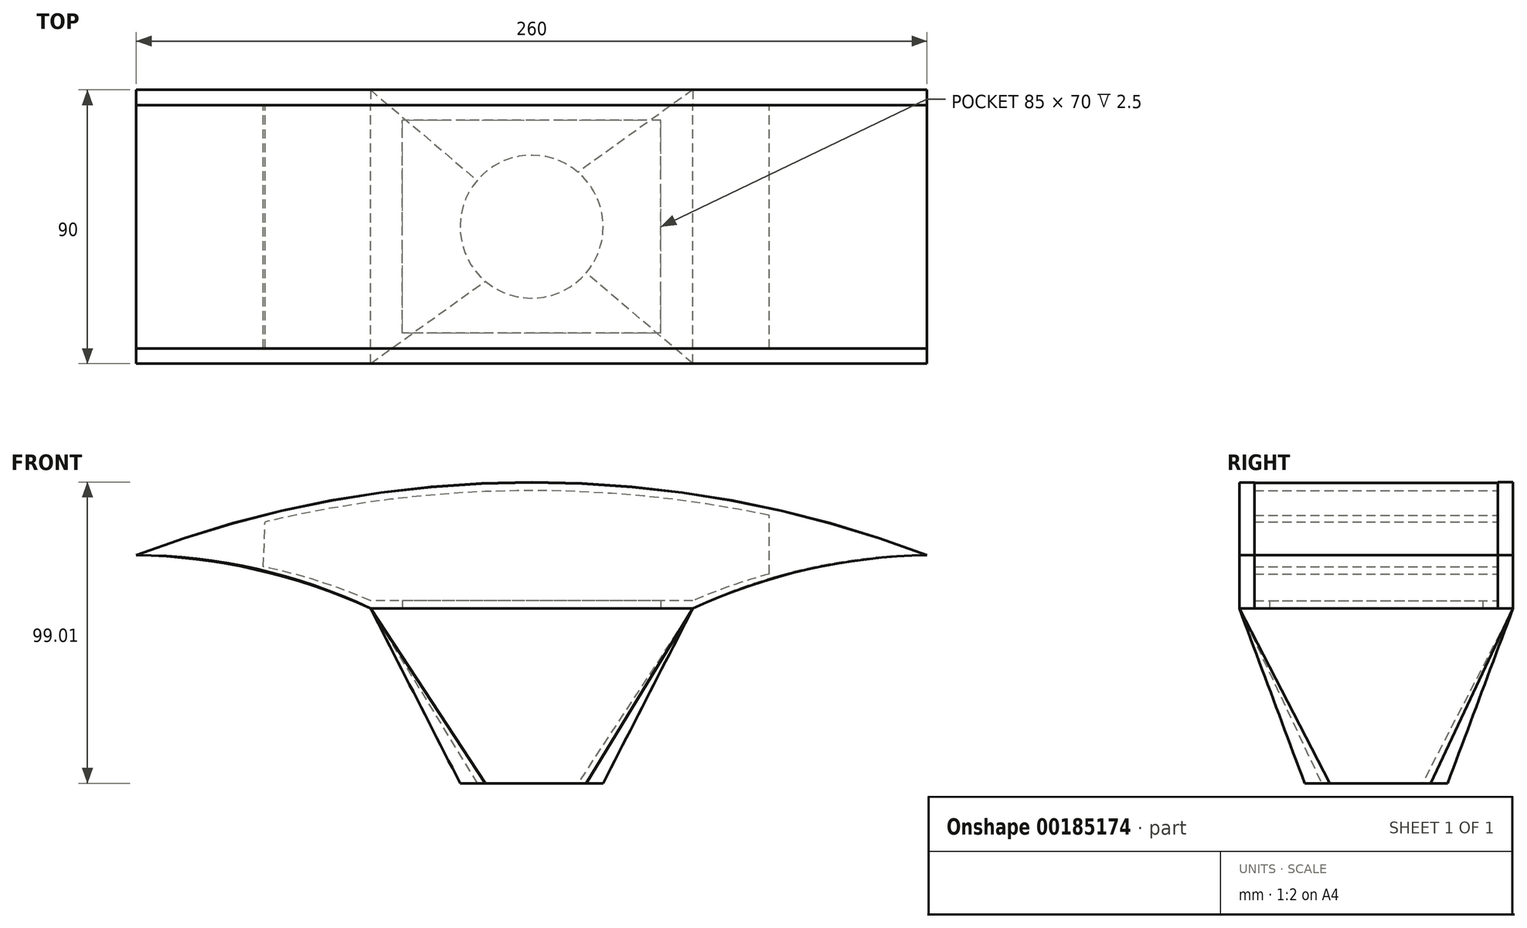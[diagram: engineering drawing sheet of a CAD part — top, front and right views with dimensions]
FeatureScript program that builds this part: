
annotation { "Feature Type Name" : "Feature", "Feature Type Description" : "" }
export const myFeature = defineFeature(function(context is Context, id is Id, definition is map)
    precondition{}
    {
        {
            var Q0;
            Q0=qCreatedBy(makeId("Front.planeOp"),FACE);
            var sketch = newSketch(context, id + "F0", { "sketchPlane" : qUnion([Q0])});
            skLineSegment(sketch, "E0.bottom", {"start": v(53, 15) * mm, "end": v(-53, 15) * mm, "construction": true});
            skLineSegment(sketch, "E0.top", {"start": v(53, -15) * mm, "end": v(-53, -15) * mm, "construction": true});
            skPoint(sketch, "E0.middle", {"position": v(0, 0) * mm});
            skCircle(sketch, "E1", {"center": v(-53, 0) * mm, "radius": 12.5 * mm, "construction": true});
            skCircle(sketch, "E2", {"center": v(53, 0) * mm, "radius": 12.5 * mm, "construction": true});
            skLineSegment(sketch, "E3", {"start": v(0, 15) * mm, "end": v(0, -70) * mm, "construction": true});
            skPoint(sketch, "E3.endSnap0", {"position": v(0, -15) * mm});
            skLineSegment(sketch, "E4.bottom", {"start": v(23.75, -70) * mm, "end": v(-23.75, -70) * mm});
            skLineSegment(sketch, "E4.top", {"start": v(23.75, -70) * mm, "end": v(-23.75, -70) * mm, "construction": true});
            skLineSegment(sketch, "E4.left", {"start": v(23.75, -70) * mm, "end": v(23.75, -70) * mm});
            skLineSegment(sketch, "E4.right", {"start": v(-23.75, -70) * mm, "end": v(-23.75, -70) * mm});
            skPoint(sketch, "E4.middle", {"position": v(0, -70) * mm});
            skArc(sketch, "E5", {"start": v(-23.75, -70) * mm, "mid": v(-31.52, -38.85) * mm, "end": v(-53, -15) * mm, "construction": true});
            skArc(sketch, "E6", {"start": v(53, -15) * mm, "mid": v(31.52, -38.85) * mm, "end": v(23.75, -70) * mm, "construction": true});
            skLineSegment(sketch, "E7", {"start": v(0, 0) * mm, "end": v(125, 0) * mm, "construction": true});
            skLineSegment(sketch, "E8", {"start": v(0, 0) * mm, "end": v(-125, 0) * mm, "construction": true});
            skArc(sketch, "E9", {"start": v(-53, -15) * mm, "mid": v(-70.33, -8.49) * mm, "end": v(-88.23, -3.79) * mm});
            skArc(sketch, "E10", {"start": v(78.13, -6.2) * mm, "mid": v(65.4, -10.13) * mm, "end": v(53, -15) * mm});
            skArc(sketch, "E11", {"start": v(78.08, 13.09) * mm, "mid": v(-4.9, 21.2) * mm, "end": v(-87.63, 10.95) * mm});
            skLineSegment(sketch, "E12.top", {"start": v(53, -17.5) * mm, "end": v(-53, -17.5) * mm});
            skLineSegment(sketch, "E13", {"start": v(125, 0) * mm, "end": v(130, 0) * mm, "construction": true});
            skArc(sketch, "E14", {"start": v(-53, -17.5) * mm, "mid": v(-90.52, -4.43) * mm, "end": v(-130, 0) * mm});
            skArc(sketch, "E15", {"start": v(130, 0) * mm, "mid": v(90.52, -4.43) * mm, "end": v(53, -17.5) * mm});
            skArc(sketch, "E16", {"start": v(130, 0) * mm, "mid": v(0, 23.82) * mm, "end": v(-130, 0) * mm});
            skLineSegment(sketch, "E17", {"start": v(-53, -15) * mm, "end": v(53, -15) * mm, "construction": true});
            skLineSegment(sketch, "E18", {"start": v(78.13, -6.2) * mm, "end": v(78.08, 13.09) * mm});
            skLineSegment(sketch, "E19", {"start": v(-88.23, -3.79) * mm, "end": v(-87.63, 10.95) * mm});
            skLineSegment(sketch, "E20.trimOffspring", {"start": v(53, -15) * mm, "end": v(53, -17.5) * mm, "construction": true});
            skLineSegment(sketch, "E21.trimOffspring", {"start": v(-53, -15) * mm, "end": v(-53, -17.5) * mm});
            skLineSegment(sketch, "E22.trimOffspring", {"start": v(-88.07, 0) * mm, "end": v(-130, 0) * mm, "construction": true});
            skPoint(sketch, "E12.bottom.end.orphan", {"position": v(-53, 17.5) * mm});
            skPoint(sketch, "E12.left.start.orphan", {"position": v(53, 17.5) * mm});
            skLineSegment(sketch, "E23", {"start": v(53, -15) * mm, "end": v(-53, -15) * mm});
            skSolve(sketch);
        }
        {
            var Q0;
            Q0 = qSketchRegion(id + "F0", true);
            extrude(context, id + "F1", {"entities" : qUnion([Q0]), "depth" : 80 * mm});
        }
        {
            var Q0;
            Q0=makeQuery(id+"F1.opExtrude","CAP_FACE",FACE,{"disambiguationData":[OSD([sQuery(id+"F0.wireOp",EDGE,"E9"),sQuery(id+"F0.wireOp",EDGE,"E10"),sQuery(id+"F0.wireOp",EDGE,"E11"),sQuery(id+"F0.wireOp",EDGE,"E12.top"),sQuery(id+"F0.wireOp",EDGE,"E14"),sQuery(id+"F0.wireOp",EDGE,"E15"),sQuery(id+"F0.wireOp",EDGE,"E16"),sQuery(id+"F0.wireOp",EDGE,"E18"),sQuery(id+"F0.wireOp",EDGE,"E19"),sQuery(id+"F0.wireOp",EDGE,"E23")])],"isStart":false});
            var sketch = newSketch(context, id + "F2", { "sketchPlane" : qUnion([Q0])});
            skArc(sketch, "E24", {"start": v(130, 0) * mm, "mid": v(0, 23.88) * mm, "end": v(-130, 0) * mm});
            skArc(sketch, "E25", {"start": v(-53, -17.5) * mm, "mid": v(-90.53, -4.49) * mm, "end": v(-130, 0) * mm});
            skArc(sketch, "E26", {"start": v(130, 0) * mm, "mid": v(90.58, -4.72) * mm, "end": v(53, -17.5) * mm});
            skLineSegment(sketch, "E27", {"start": v(-53, -17.5) * mm, "end": v(53, -17.5) * mm});
            skSolve(sketch);
        }
        {
            var Q0;
            Q0 = qSketchRegion(id + "F2", true);
            extrude(context, id + "F3", {"entities" : qUnion([Q0]), "operationType" : NewBodyOperationType.ADD, "depth" : 5 * mm});
        }
        {
            var Q0;
            Q0=makeQuery(id+"F1.opExtrude","CAP_FACE",FACE,{"disambiguationData":[OSD([sQuery(id+"F0.wireOp",EDGE,"E9"),sQuery(id+"F0.wireOp",EDGE,"E10"),sQuery(id+"F0.wireOp",EDGE,"E11"),sQuery(id+"F0.wireOp",EDGE,"E12.top"),sQuery(id+"F0.wireOp",EDGE,"E14"),sQuery(id+"F0.wireOp",EDGE,"E15"),sQuery(id+"F0.wireOp",EDGE,"E16"),sQuery(id+"F0.wireOp",EDGE,"E18"),sQuery(id+"F0.wireOp",EDGE,"E19"),sQuery(id+"F0.wireOp",EDGE,"E23")])],"isStart":true});
            var sketch = newSketch(context, id + "F4", { "sketchPlane" : qUnion([Q0])});
            skArc(sketch, "E28", {"start": v(130, 0) * mm, "mid": v(0, 24.01) * mm, "end": v(-130, 0) * mm});
            skArc(sketch, "E29", {"start": v(-53, -17.5) * mm, "mid": v(-90.58, -4.72) * mm, "end": v(-130, 0) * mm});
            skArc(sketch, "E30", {"start": v(130, 0) * mm, "mid": v(90.6, -4.77) * mm, "end": v(53, -17.5) * mm});
            skLineSegment(sketch, "E31", {"start": v(-53, -17.5) * mm, "end": v(53, -17.5) * mm});
            skSolve(sketch);
        }
        {
            var Q0;
            Q0 = qSketchRegion(id + "F4", true);
            extrude(context, id + "F5", {"entities" : qUnion([Q0]), "operationType" : NewBodyOperationType.ADD, "depth" : 5 * mm});
        }
        {
            var Q0;
            Q0=makeQuery(id+"F5.boolean.opBoolean","MERGE",FACE,{"derivedFrom":[makeQuery(id+"F3.boolean.opBoolean","MERGE",FACE,{"derivedFrom":[makeQuery(id+"F1.opExtrude","SWEPT_FACE",FACE,{"disambiguationData":[OSD([sQuery(id+"F0.wireOp",EDGE,"E12.top")])]}),makeQuery(id+"F3.opExtrude","SWEPT_FACE",FACE,{"disambiguationData":[OSD([sQuery(id+"F2.wireOp",EDGE,"E27")])]})]}),makeQuery(id+"F5.opExtrude","SWEPT_FACE",FACE,{"disambiguationData":[OSD([sQuery(id+"F4.wireOp",EDGE,"E31")])]})]});
            var sketch = newSketch(context, id + "F6", { "sketchPlane" : qUnion([Q0])});
            skLineSegment(sketch, "E32.bottom", {"start": v(42.5, 75) * mm, "end": v(-42.5, 75) * mm});
            skLineSegment(sketch, "E32.top", {"start": v(42.5, 5) * mm, "end": v(-42.5, 5) * mm});
            skLineSegment(sketch, "E32.left", {"start": v(42.5, 75) * mm, "end": v(42.5, 5) * mm});
            skLineSegment(sketch, "E32.right", {"start": v(-42.5, 75) * mm, "end": v(-42.5, 5) * mm});
            skPoint(sketch, "E32.middle", {"position": v(0, 40) * mm});
            skSolve(sketch);
        }
        {
            var Q0;
            Q0 = qSketchRegion(id + "F6", true);
            extrude(context, id + "F7", {"entities" : qUnion([Q0]), "operationType" : NewBodyOperationType.REMOVE, "oppositeDirection" : true, "depth" : 25 * mm});
        }
        {
            var Q0;
            Q0=qCreatedBy(makeId("Top.planeOp"),FACE);
            cPlane(context, id + "F8", {"entities" : qUnion([Q0]), "cplaneType" : CPlaneType.OFFSET, "offset" : 75 * mm, "oppositeDirection" : true, "width" : 150 * mm, "height" : 150 * mm});
        }
        {
            var Q0;
            Q0=qCreatedBy(id+"F8.planeOp",FACE);
            var sketch = newSketch(context, id + "F9", { "sketchPlane" : qUnion([Q0])});
            skCircle(sketch, "E33", {"center": v(0, -40) * mm, "radius": 23.5 * mm});
            skSolve(sketch);
        }
        {
            var Q0;
            Q0=makeQuery(id+"F5.boolean.opBoolean","MERGE",FACE,{"derivedFrom":[makeQuery(id+"F3.boolean.opBoolean","MERGE",FACE,{"derivedFrom":[makeQuery(id+"F1.opExtrude","SWEPT_FACE",FACE,{"disambiguationData":[OSD([sQuery(id+"F0.wireOp",EDGE,"E12.top")])]}),makeQuery(id+"F3.opExtrude","SWEPT_FACE",FACE,{"disambiguationData":[OSD([sQuery(id+"F2.wireOp",EDGE,"E27")])]})]}),makeQuery(id+"F5.opExtrude","SWEPT_FACE",FACE,{"disambiguationData":[OSD([sQuery(id+"F4.wireOp",EDGE,"E31")])]})]});
            var sketch = newSketch(context, id + "F10", { "sketchPlane" : qUnion([Q0])});
            skLineSegment(sketch, "E34.bottom", {"start": v(53, -5) * mm, "end": v(-53, -5) * mm});
            skLineSegment(sketch, "E34.top", {"start": v(53, 85) * mm, "end": v(-53, 85) * mm});
            skLineSegment(sketch, "E34.left", {"start": v(53, -5) * mm, "end": v(53, 85) * mm});
            skLineSegment(sketch, "E34.right", {"start": v(-53, -5) * mm, "end": v(-53, 85) * mm});
            skSolve(sketch);
        }
        {
            var Q1;
            Q1 = qSketchRegion(id + "F10", true);
            var Q2;
            Q2 = qSketchRegion(id + "F9", true);
            loft(context, id + "F11", {"operationType" : NewBodyOperationType.ADD, "sheetProfilesArray" : [{ "sheetProfileEntities" : qUnion([Q1]) }, { "sheetProfileEntities" : qUnion([Q2]) }]});
        }
    });
